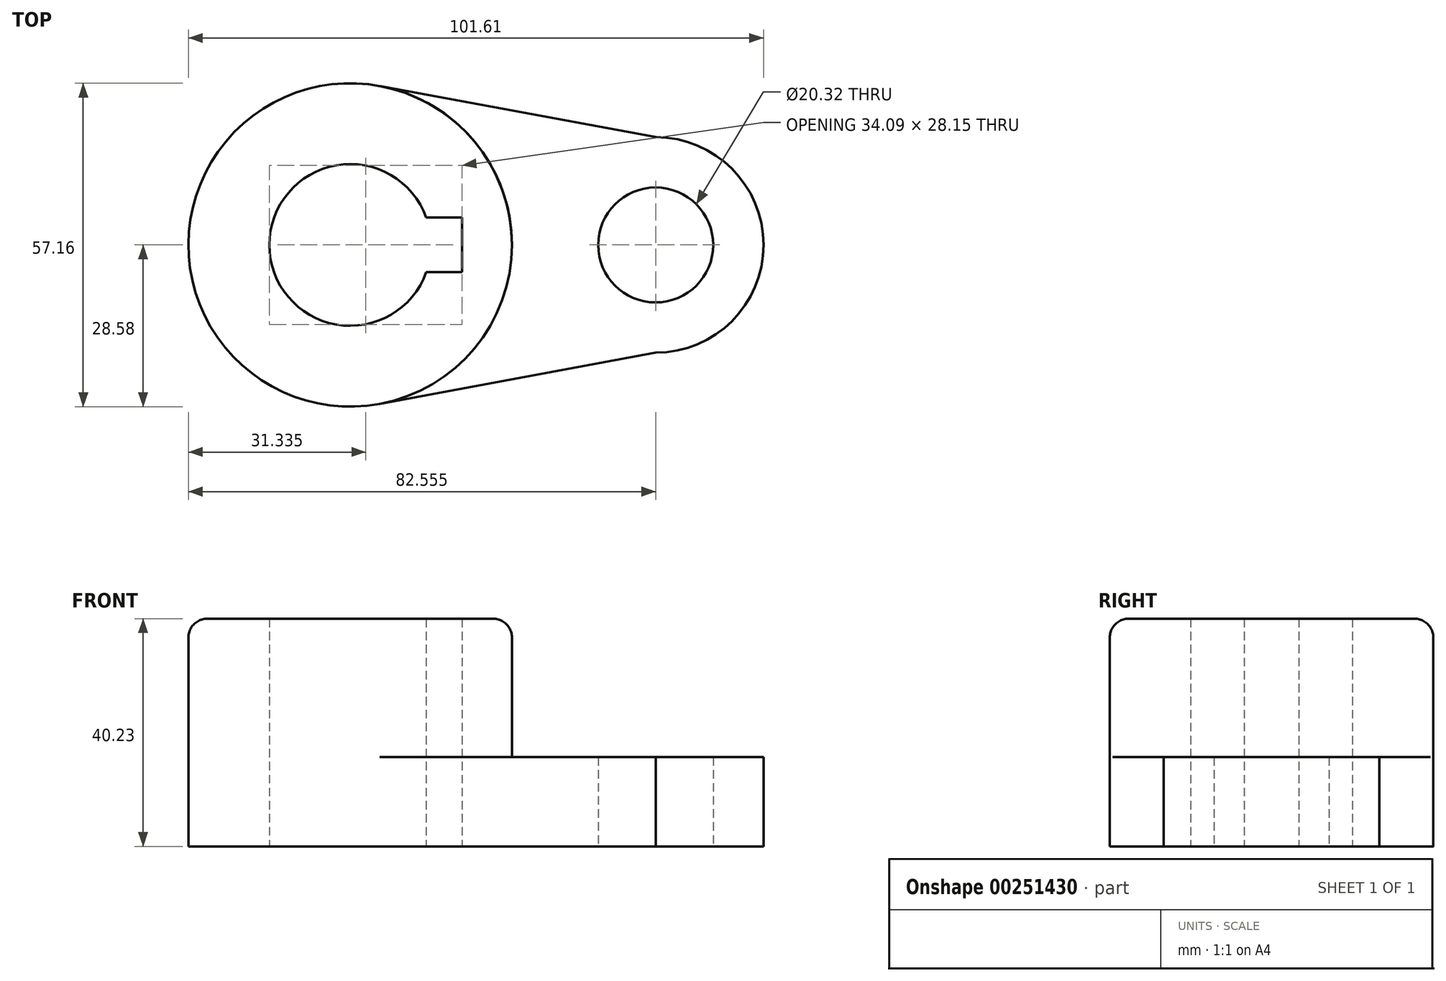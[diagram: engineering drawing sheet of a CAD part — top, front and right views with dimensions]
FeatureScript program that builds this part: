
annotation { "Feature Type Name" : "Feature", "Feature Type Description" : "" }
export const myFeature = defineFeature(function(context is Context, id is Id, definition is map)
    precondition{}
    {
        {
            var Q0;
            Q0=qCreatedBy(makeId("Top.planeOp"),FACE);
            var sketch = newSketch(context, id + "F0", { "sketchPlane" : qUnion([Q0])});
            skCircle(sketch, "E0", {"center": v(53.98, 0) * mm, "radius": 10.16 * mm});
            skCircle(sketch, "E1", {"center": v(0, 0) * mm, "radius": 28.58 * mm});
            skCircle(sketch, "E2", {"center": v(53.98, 0) * mm, "radius": 19.05 * mm});
            skPoint(sketch, "E3.visualSharp", {"position": v(33.04, -28.58) * mm});
            skLineSegment(sketch, "E4", {"start": v(0, 0) * mm, "end": v(53.98, 0) * mm, "construction": true});
            skLineSegment(sketch, "E5", {"start": v(53.98, 19.05) * mm, "end": v(5.21, 28.1) * mm});
            skLineSegment(sketch, "E6", {"start": v(53.98, -19.05) * mm, "end": v(5.21, -28.1) * mm});
            skArc(sketch, "E7", {"start": v(13.45, 4.83) * mm, "mid": v(-14.29, 0) * mm, "end": v(13.45, -4.83) * mm});
            skLineSegment(sketch, "E8.bottom", {"start": v(19.8, -4.83) * mm, "end": v(13.45, -4.83) * mm});
            skLineSegment(sketch, "E8.top", {"start": v(19.8, 4.83) * mm, "end": v(13.45, 4.83) * mm});
            skLineSegment(sketch, "E8.left", {"start": v(19.8, -4.83) * mm, "end": v(19.8, 4.83) * mm});
            skPoint(sketch, "E8.right.end.orphan", {"position": v(-19.8, 4.83) * mm});
            skPoint(sketch, "E8.right.start.orphan", {"position": v(-19.8, -4.83) * mm});
            skSolve(sketch);
        }
        {
            var Q0;
            Q0=makeQuery(id+"F0.imprint","IMPRINT",FACE,{"disambiguationData":[TD([[makeQuery(id+"F0.imprint","IMPRINT",EDGE,{"derivedFrom":sQuery(id+"F0.wireOp",EDGE,"OW2BRuVo-h5eh-Ojls-tUQz-FdrJ9uoOWhWJ")}),-1.0]])]});
            var Q1;
            Q1=makeQuery(id+"F0.imprint","IMPRINT",FACE,{"disambiguationData":[TD([[makeQuery(id+"F0.imprint","IMPRINT",EDGE,{"derivedFrom":sQuery(id+"F0.wireOp",EDGE,"E7")}),-1.0]])]});
            extrude(context, id + "F1", {"entities" : qUnion([Q0, Q1]), "depth" : 40.23 * mm});
        }
        {
            var Q0;
            {var subQ0=sQuery(id+"F0.wireOp",EDGE,"o5OdITKO-bEnJ-2VYi-a7Jk-zIUuU5JH3HSI");var subQ1=sQuery(id+"F0.wireOp",EDGE,"E1");var subQ2=makeQuery(id+"F0.imprint","INTERSECT",VERTEX,{"disambiguationData":[OD(1.0)],"derivedFrom":[subQ1,subQ0]});Q0=makeQuery(id+"F0.imprint","IMPRINT",FACE,{"disambiguationData":[TD([[makeQuery(id+"F0.imprint","IMPRINT",EDGE,{"disambiguationData":[TD([[subQ2,1.0]])],"derivedFrom":subQ1}),-1.0]])]});}
            var Q1;
            Q1=makeQuery(id+"F0.imprint","IMPRINT",FACE,{"disambiguationData":[TD([[makeQuery(id+"F0.imprint","IMPRINT",EDGE,{"derivedFrom":sQuery(id+"F0.wireOp",EDGE,"E0")}),-1.0]])]});
            extrude(context, id + "F2", {"entities" : qUnion([Q0, Q1]), "operationType" : NewBodyOperationType.ADD, "depth" : 15.77 * mm});
        }
        {
            var Q0;
            {var subQ0=sQuery(id+"F0.wireOp",EDGE,"E1");Q0=makeQuery(id+"F1.opExtrude","CAP_EDGE",EDGE,{"disambiguationData":[OSD([subQ0]),TDD([makeQuery(id+"F0.imprint","IMPRINT",EDGE,{"disambiguationData":[TD([[makeQuery(id+"F0.imprint","INTERSECT",VERTEX,{"disambiguationData":[OD(0.0)],"derivedFrom":[subQ0,sQuery(id+"F0.wireOp",EDGE,"SRnHb5uK-vhAm-8B8o-SrwD-EHZrL22LgCVp")]}),1.0]])],"derivedFrom":subQ0})])],"isStart":false});}
            var Q1;
            Q1=makeQuery(id+"F1.opExtrude","CAP_EDGE",EDGE,{"disambiguationData":[OSD([sQuery(id+"F0.wireOp",EDGE,"SRnHb5uK-vhAm-8B8o-SrwD-EHZrL22LgCVp")])],"isStart":false});
            var Q2;
            {var subQ0=sQuery(id+"F0.wireOp",EDGE,"E1");Q2=makeQuery(id+"F1.opExtrude","CAP_EDGE",EDGE,{"disambiguationData":[OSD([subQ0]),TDD([makeQuery(id+"F0.imprint","IMPRINT",EDGE,{"disambiguationData":[TD([[makeQuery(id+"F0.imprint","INTERSECT",VERTEX,{"disambiguationData":[OD(1.0)],"derivedFrom":[subQ0,sQuery(id+"F0.wireOp",EDGE,"o5OdITKO-bEnJ-2VYi-a7Jk-zIUuU5JH3HSI")]}),1.0]])],"derivedFrom":subQ0})])],"isStart":false});}
            var Q3;
            Q3=makeQuery(id+"F1.opExtrude","CAP_EDGE",EDGE,{"disambiguationData":[OSD([sQuery(id+"F0.wireOp",EDGE,"o5OdITKO-bEnJ-2VYi-a7Jk-zIUuU5JH3HSI")])],"isStart":false});
            fillet(context, id + "F3", {"entities" : qUnion([Q0, Q1, Q2, Q3]), "radius" : 3.3 * mm, "tangentPropagation" : true, "allowEdgeOverflow" : false});
        }
    });
